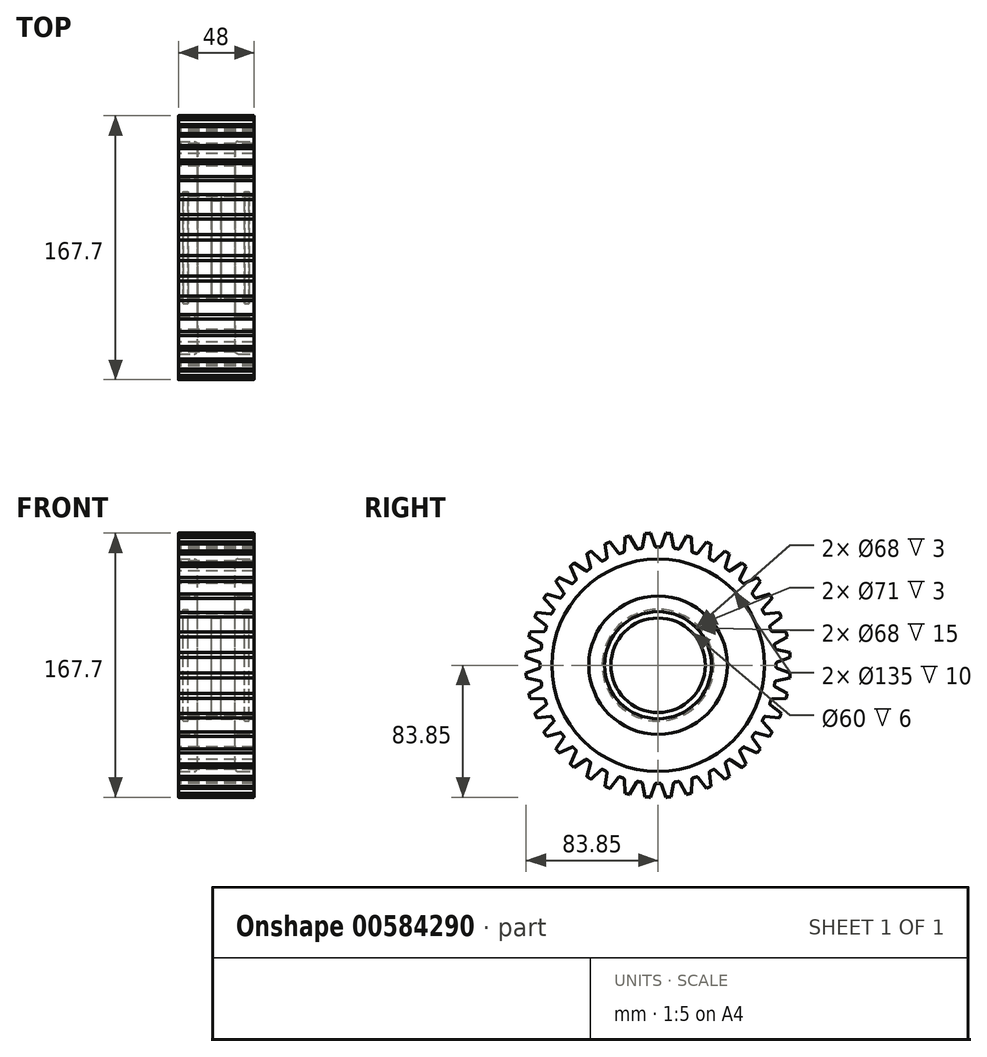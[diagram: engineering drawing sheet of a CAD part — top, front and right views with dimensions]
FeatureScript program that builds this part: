
annotation { "Feature Type Name" : "Feature", "Feature Type Description" : "" }
export const myFeature = defineFeature(function(context is Context, id is Id, definition is map)
    precondition{}
    {
        {
            var Q0;
            Q0=qCreatedBy(makeId("Front.planeOp"),FACE);
            var sketch = newSketch(context, id + "F0", { "sketchPlane" : qUnion([Q0])});
            skLineSegment(sketch, "E0.bottom", {"start": v(0, 0) * mm, "end": v(-24, 0) * mm, "construction": true});
            skLineSegment(sketch, "E0.top", {"start": v(0, 84) * mm, "end": v(-24, 84) * mm});
            skLineSegment(sketch, "E0.left", {"start": v(0, 0) * mm, "end": v(0, 84) * mm, "construction": true});
            skLineSegment(sketch, "E0.right", {"start": v(-24, 34) * mm, "end": v(-24, 44) * mm});
            skLineSegment(sketch, "E1", {"start": v(-24, 34) * mm, "end": v(-21, 34) * mm});
            skLineSegment(sketch, "E2", {"start": v(-21, 34) * mm, "end": v(-21, 35.5) * mm});
            skLineSegment(sketch, "E3", {"start": v(-21, 35.5) * mm, "end": v(-18, 35.5) * mm});
            skLineSegment(sketch, "E4", {"start": v(-18, 35.5) * mm, "end": v(-18, 34) * mm});
            skLineSegment(sketch, "E5", {"start": v(-18, 34) * mm, "end": v(-3, 34) * mm});
            skLineSegment(sketch, "E6", {"start": v(-3, 34) * mm, "end": v(-3, 30) * mm});
            skLineSegment(sketch, "E7", {"start": v(-3, 30) * mm, "end": v(0, 30) * mm});
            skLineSegment(sketch, "E8", {"start": v(-24, 44) * mm, "end": v(-14, 44) * mm});
            skLineSegment(sketch, "E9", {"start": v(-12, 46) * mm, "end": v(-12, 65.5) * mm});
            skLineSegment(sketch, "E10", {"start": v(-14, 67.5) * mm, "end": v(-24, 67.5) * mm});
            skLineSegment(sketch, "E11.trimOffspring", {"start": v(-24, 67.5) * mm, "end": v(-24, 84) * mm});
            skPoint(sketch, "E12.visualSharp", {"position": v(-12, 67.5) * mm});
            skArc(sketch, "E12.filletArc", {"start": v(-12, 65.5) * mm, "mid": v(-12.59, 66.91) * mm, "end": v(-14, 67.5) * mm});
            skPoint(sketch, "E13.visualSharp", {"position": v(-12, 44) * mm});
            skArc(sketch, "E13.filletArc", {"start": v(-14, 44) * mm, "mid": v(-12.59, 44.59) * mm, "end": v(-12, 46) * mm});
            skLineSegment(sketch, "E14.MirrorCS", {"start": v(0, 84) * mm, "end": v(24, 84) * mm});
            skLineSegment(sketch, "E15.MirrorCS", {"start": v(24, 67.5) * mm, "end": v(24, 84) * mm});
            skLineSegment(sketch, "E16.MirrorCS", {"start": v(14, 67.5) * mm, "end": v(24, 67.5) * mm});
            skArc(sketch, "E17.MirrorCS", {"start": v(12, 65.5) * mm, "mid": v(12.59, 66.91) * mm, "end": v(14, 67.5) * mm});
            skLineSegment(sketch, "E18.MirrorCS", {"start": v(12, 46) * mm, "end": v(12, 65.5) * mm});
            skArc(sketch, "E19.MirrorCS", {"start": v(14, 44) * mm, "mid": v(12.59, 44.59) * mm, "end": v(12, 46) * mm});
            skLineSegment(sketch, "E20.MirrorCS", {"start": v(24, 44) * mm, "end": v(14, 44) * mm});
            skLineSegment(sketch, "E21.MirrorCS", {"start": v(24, 34) * mm, "end": v(24, 44) * mm});
            skLineSegment(sketch, "E22.MirrorCS", {"start": v(24, 34) * mm, "end": v(21, 34) * mm});
            skLineSegment(sketch, "E23.MirrorCS", {"start": v(21, 34) * mm, "end": v(21, 35.5) * mm});
            skLineSegment(sketch, "E24.MirrorCS", {"start": v(21, 35.5) * mm, "end": v(18, 35.5) * mm});
            skLineSegment(sketch, "E25.MirrorCS", {"start": v(18, 35.5) * mm, "end": v(18, 34) * mm});
            skLineSegment(sketch, "E26.MirrorCS", {"start": v(18, 34) * mm, "end": v(3, 34) * mm});
            skLineSegment(sketch, "E27.MirrorCS", {"start": v(3, 34) * mm, "end": v(3, 30) * mm});
            skLineSegment(sketch, "E28.MirrorCS", {"start": v(3, 30) * mm, "end": v(0, 30) * mm});
            skSolve(sketch);
        }
        {
            var Q0;
            Q0 = qSketchRegion(id + "F0", true);
            var Q1;
            Q1=sQuery(id+"F0.wireOp",EDGE,"E0.bottom");
            revolve(context, id + "F1", {"entities" : qUnion([Q0]), "axis" : qUnion([Q1]), "revolveType" : RevolveType.FULL});
        }
        {
            var Q0;
            Q0=qCreatedBy(makeId("Right.planeOp"),FACE);
            var sketch = newSketch(context, id + "F2", { "sketchPlane" : qUnion([Q0])});
            skArc(sketch, "E29", {"start": v(1.04, 75) * mm, "mid": v(0, 75) * mm, "end": v(-1.04, 75) * mm});
            skLineSegment(sketch, "E30", {"start": v(0, 0) * mm, "end": v(0, 86.62) * mm, "construction": true});
            skArc(sketch, "E31", {"start": v(4.98, 83.85) * mm, "mid": v(0, 84) * mm, "end": v(-4.98, 83.85) * mm});
            skLineSegment(sketch, "E32", {"start": v(2, 75.65) * mm, "end": v(4.98, 83.85) * mm});
            skLineSegment(sketch, "E33.MirrorCS", {"start": v(-2, 75.65) * mm, "end": v(-4.98, 83.85) * mm});
            skPoint(sketch, "E34.visualSharp", {"position": v(-1.75, 74.98) * mm});
            skArc(sketch, "E34.filletArc", {"start": v(-2, 75.65) * mm, "mid": v(-1.62, 75.17) * mm, "end": v(-1.04, 75) * mm});
            skPoint(sketch, "E35.visualSharp", {"position": v(1.75, 74.98) * mm});
            skArc(sketch, "E35.filletArc", {"start": v(1.04, 75) * mm, "mid": v(1.62, 75.17) * mm, "end": v(2, 75.65) * mm});
            skSolve(sketch);
        }
        {
            var Q0;
            Q0 = qSketchRegion(id + "F2", true);
            extrude(context, id + "F3", {"entities" : qUnion([Q0]), "operationType" : NewBodyOperationType.REMOVE, "endBound" : BoundingType.SYMMETRIC, "depth" : 50 * mm, "offsetDistance" : 25 * mm});
        }
        {
            var Q0;
            Q0=makeQuery(id+"F3.boolean.opBoolean","COPY",FACE,{"derivedFrom":makeQuery(id+"F3.opExtrude","SWEPT_FACE",FACE,{"disambiguationData":[OSD([sQuery(id+"F2.wireOp",EDGE,"E32")])]})});
            var Q1;
            Q1=makeQuery(id+"F3.boolean.opBoolean","COPY",FACE,{"derivedFrom":makeQuery(id+"F3.opExtrude","SWEPT_FACE",FACE,{"disambiguationData":[OSD([sQuery(id+"F2.wireOp",EDGE,"E35.filletArc")])]})});
            var Q2;
            Q2=makeQuery(id+"F3.boolean.opBoolean","COPY",FACE,{"derivedFrom":makeQuery(id+"F3.opExtrude","SWEPT_FACE",FACE,{"disambiguationData":[OSD([sQuery(id+"F2.wireOp",EDGE,"E29")])]})});
            var Q3;
            Q3=makeQuery(id+"F3.boolean.opBoolean","COPY",FACE,{"derivedFrom":makeQuery(id+"F3.opExtrude","SWEPT_FACE",FACE,{"disambiguationData":[OSD([sQuery(id+"F2.wireOp",EDGE,"E34.filletArc")])]})});
            var Q4;
            Q4=makeQuery(id+"F3.boolean.opBoolean","COPY",FACE,{"derivedFrom":makeQuery(id+"F3.opExtrude","SWEPT_FACE",FACE,{"disambiguationData":[OSD([sQuery(id+"F2.wireOp",EDGE,"E33.MirrorCS")])]})});
            var Q5;
            Q5=makeQuery(id+"F1.opRevolve","SWEPT_FACE",FACE,{"disambiguationData":[OSD([sQuery(id+"F0.wireOp",EDGE,"E0.top"),sQuery(id+"F0.wireOp",EDGE,"E14.MirrorCS")])]});
            circularPattern(context, id + "F4", {"patternType" : PatternType.FACE, "faces" : qUnion([Q0, Q1, Q2, Q3, Q4]), "axis" : qUnion([Q5]), "angle" : 9 * degree, "instanceCount" : 40});
        }
    });
